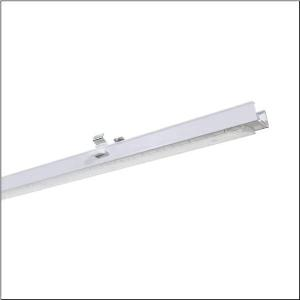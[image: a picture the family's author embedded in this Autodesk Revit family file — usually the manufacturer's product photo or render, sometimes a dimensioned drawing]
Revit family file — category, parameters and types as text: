
# Revit family: trunking_flex_31_51re11mb48b
name_source: partatom
category: Lighting Fixtures
units: mm (PartAtom-declared; Revit-internal decimal feet)

## family parameters
Cut with Voids When Loaded = No
Host = Face
Light Source = No
Part Type = Normal
Room Calculation Point = No
Round Connector Dimension = Use Diameter
Shared = No

## types (1)
- --- (1 x LED, 8000 lm, 50 W, 4000K)
    Apparent Load = 50 VA
    CIE Flux Codes = 83 93 98 100 100
    Color Rendering = 80
    Color Temperature = 4000K
    Default Elevation = 1800 mm
    Description = Trunking Flex 31, luminaire insert, of extruded aluminium section, coated, traffic white (RAL 9016), length: 1.472mm, width: 91mm, height: 53mm, LED rated luminous flux: 8.000lm, light colour: 840, control gear: ON/OFF Multilumen, with system connector: socket, mains connection: 220..240V, AC, 50/60Hz, rated input power: 50W, luminous flux adjustable on luminaire in four steps (4130/5610/6850/8000lm), connected load according to luminous flux setting (25/34/42/50W), primary light control with lens, of plastic, primary optical cover: cover, of PMMA, light emission: direct distribution, protection rating (complete): IP20, insulation class (complete): insulation class I (protective earthing), certification: CE, UKCA, impact resistance: IK02, permissible ambient temperature for indoor applications: -20..+40°C, packaging unit: 1 piece
    Height = 58 mm
    Lamp = 1 x LED
    Lamp Light Flux = 8000 lm
    Lamp Power = 50 W
    Lamp count = 1
    Length = 1472 mm
    Luminous efficacy = 160 lm/W
    Manufacturer = Siteco
    ModVariant = No
    Model = 51RE11MB48B
    Mounting Place = Ceiling
    Mounting Type = Pendant
    Number of Poles = 1
    OnlyDefault = Yes
    Power Factor = 1
    Product Name = Trunking Flex 31
    Product group = luminaire insert
    ProductGroupID = 901
    Protection Class = Protection class I
    Protection Degree = IP 20
    RLX_Detail_Level = 1
    RLX_Emergency_Light_Flux = 0 lm
    RLX_Emergency_Type = 0
    RLX_Emergency_Type_DB = No
    RlxData = <blob elided: 20209 chars, md5=ea62762a>
    Socket = socket
    Standby Power = 0 W
    System Light Flux = 8000 lm
    System Power = 50 W
    Type Comments = factory setting: luminous flux: 100 % | (ON | ON) | 300 mA
    Type Image = l_1266702.jpg
    URL = http://relux.com
    VarID = @adj_018791
    Voltage = 0 V
    Weight = 0.00 kg
    Width = 65 mm

## geometry (parser evidence)
native form markers: Blend x4, Sweep x11
no freeform markers — native parametric forms only
